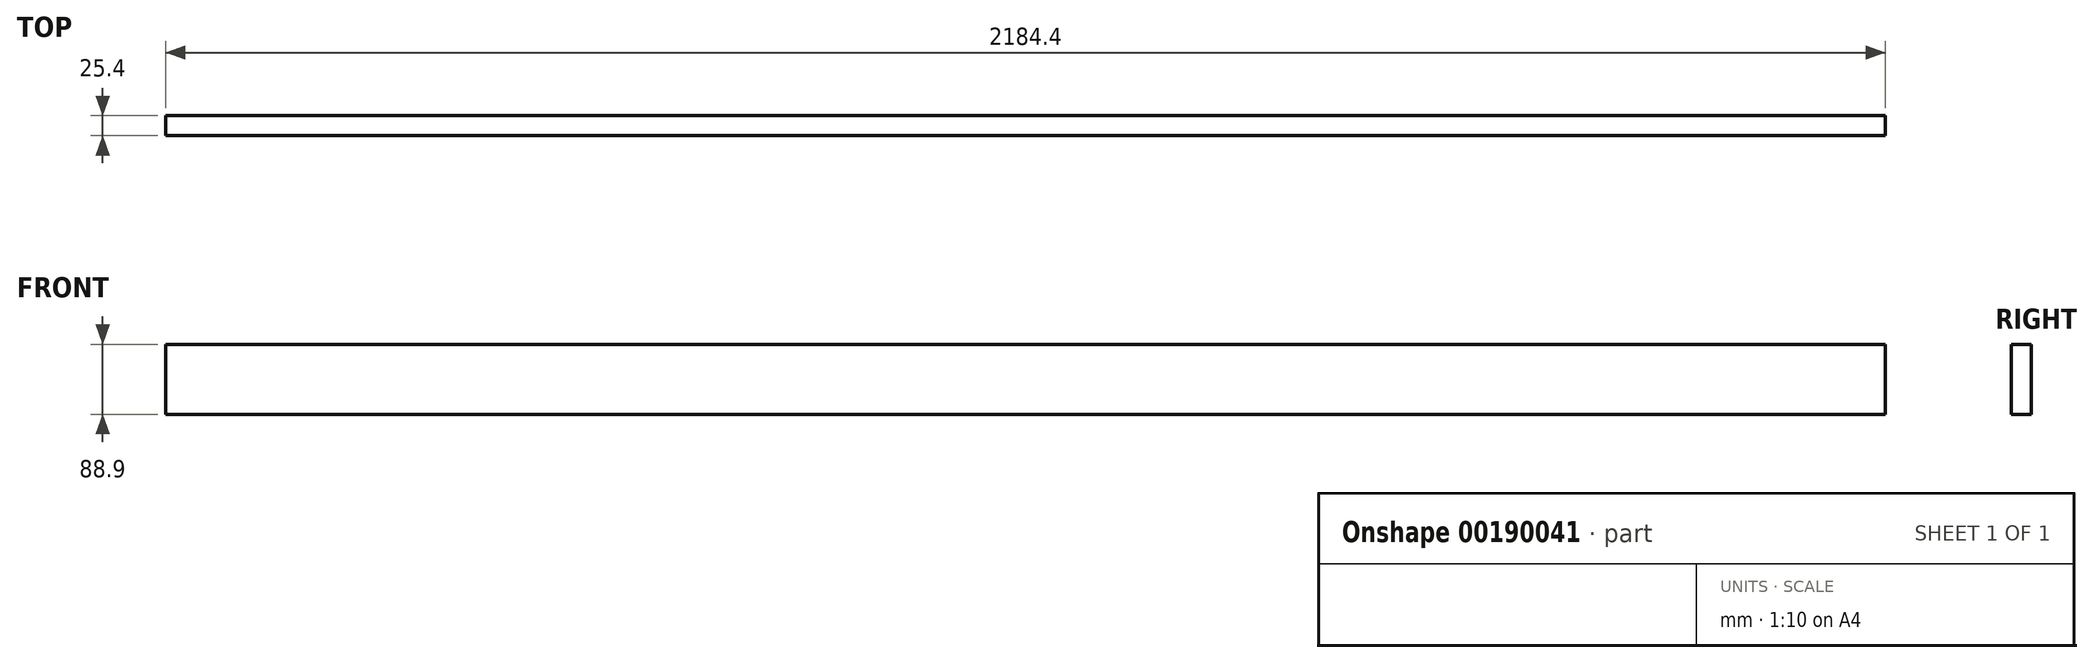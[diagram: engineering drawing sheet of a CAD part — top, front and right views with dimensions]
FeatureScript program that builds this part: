
annotation { "Feature Type Name" : "Feature", "Feature Type Description" : "" }
export const myFeature = defineFeature(function(context is Context, id is Id, definition is map)
    precondition{}
    {
        {
            var Q0;
            Q0=qCreatedBy(makeId("Front.planeOp"),FACE);
            var sketch = newSketch(context, id + "F0", { "sketchPlane" : qUnion([Q0])});
            skLineSegment(sketch, "E0.bottom", {"start": v(1092.2, 44.45) * mm, "end": v(-1092.2, 44.45) * mm});
            skLineSegment(sketch, "E0.top", {"start": v(1092.2, -44.45) * mm, "end": v(-1092.2, -44.45) * mm});
            skLineSegment(sketch, "E0.left", {"start": v(1092.2, 44.45) * mm, "end": v(1092.2, -44.45) * mm});
            skLineSegment(sketch, "E0.right", {"start": v(-1092.2, 44.45) * mm, "end": v(-1092.2, -44.45) * mm});
            skPoint(sketch, "E0.middle", {"position": v(0, 0) * mm});
            skSolve(sketch);
        }
        {
            var Q0;
            Q0 = qSketchRegion(id + "F0", true);
            extrude(context, id + "F1", {"entities" : qUnion([Q0]), "depth" : 25.4 * mm});
        }
    });
